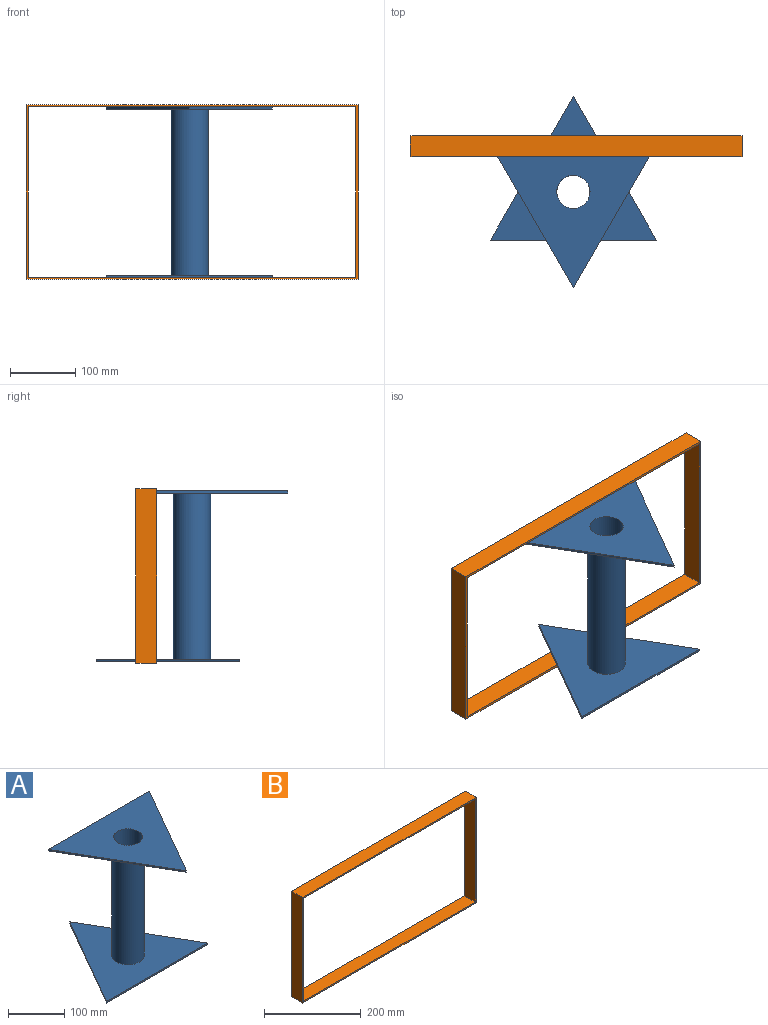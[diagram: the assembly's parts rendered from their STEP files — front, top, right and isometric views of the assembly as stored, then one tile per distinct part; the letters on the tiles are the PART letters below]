
ASSEMBLY  parts=2 mates=1
PART A: 12 faces, bbox 254x293.3x260.4 mm
  f0: plane 219.97x127mm, normal (-0.87,0.5,0), area 806.4mm2, adj f1,f3,f4,f5
  f1: plane 254x3.18mm, normal (0,-1,0), area 806.5mm2, adj f0,f3,f4,f5
  f2: cylinder r=25.4mm len=260.35mm, axis (0,0,-1), area 41550mm2, adj f5,f10
  f3: plane 219.97x127mm, normal (0.87,0.5,0), area 806.4mm2, adj f0,f1,f4,f5
  f4: plane 254x219.97mm, normal (0,0,1), area 25371mm2, adj f0,f1,f3,f6
  f5: plane 254x219.97mm, normal (0,0,-1), area 25909.4mm2, adj f0,f1,f2,f3
  f6: cylinder r=28.57mm len=254mm, axis (0,0,-1), area 45603.7mm2, adj f4,f11
  f7: plane 219.97x127mm, normal (0.87,-0.5,0), area 806.4mm2, adj f8,f9,f10,f11
  f8: plane 254x3.18mm, normal (0,1,0), area 806.5mm2, adj f7,f9,f10,f11
  f9: plane 219.97x127mm, normal (-0.87,-0.5,0), area 806.4mm2, adj f7,f8,f10,f11
  f10: plane 254x219.97mm, normal (0,0,1), area 25909.4mm2, adj f2,f7,f8,f9
  f11: plane 254x219.97mm, normal (0,0,-1), area 25371mm2, adj f6,f7,f8,f9
PART B: 10 faces, bbox 508x31.8x266.7 mm
  f0: plane 508x31.75mm, normal (0,0,1), area 16129mm2, adj f2,f4,f8,f9
  f1: plane 501.65x31.75mm, normal (0,0,-1), area 15927.4mm2, adj f3,f5,f8,f9
  f2: plane 266.7x31.75mm, normal (1,0,0), area 8467.7mm2, adj f0,f6,f8,f9
  f3: plane 260.35x31.75mm, normal (-1,0,0), area 8266.1mm2, adj f1,f7,f8,f9
  f4: plane 266.7x31.75mm, normal (-1,0,0), area 8467.7mm2, adj f0,f6,f8,f9
  f5: plane 260.35x31.75mm, normal (1,0,0), area 8266.1mm2, adj f1,f7,f8,f9
  f6: plane 508x31.75mm, normal (0,0,-1), area 16129mm2, adj f2,f4,f8,f9
  f7: plane 501.65x31.75mm, normal (0,0,1), area 15927.4mm2, adj f3,f5,f8,f9
  f8: plane 508x266.7mm, normal (0,1,0), area 4879mm2, adj f0,f1,f2,f3,f4,f5,f6,f7
  f9: plane 508x266.7mm, normal (0,-1,0), area 4879mm2, adj f0,f1,f2,f3,f4,f5,f6,f7
PLACE A t=(-253.93,-179.84,-60.12)mm
PLACE B t=(-262.58,-93.91,-0.02)mm
MATE planar A.f6 <-> B.f1  axis (0,0,1) through (-253.93,-179.84,200.23)mm
